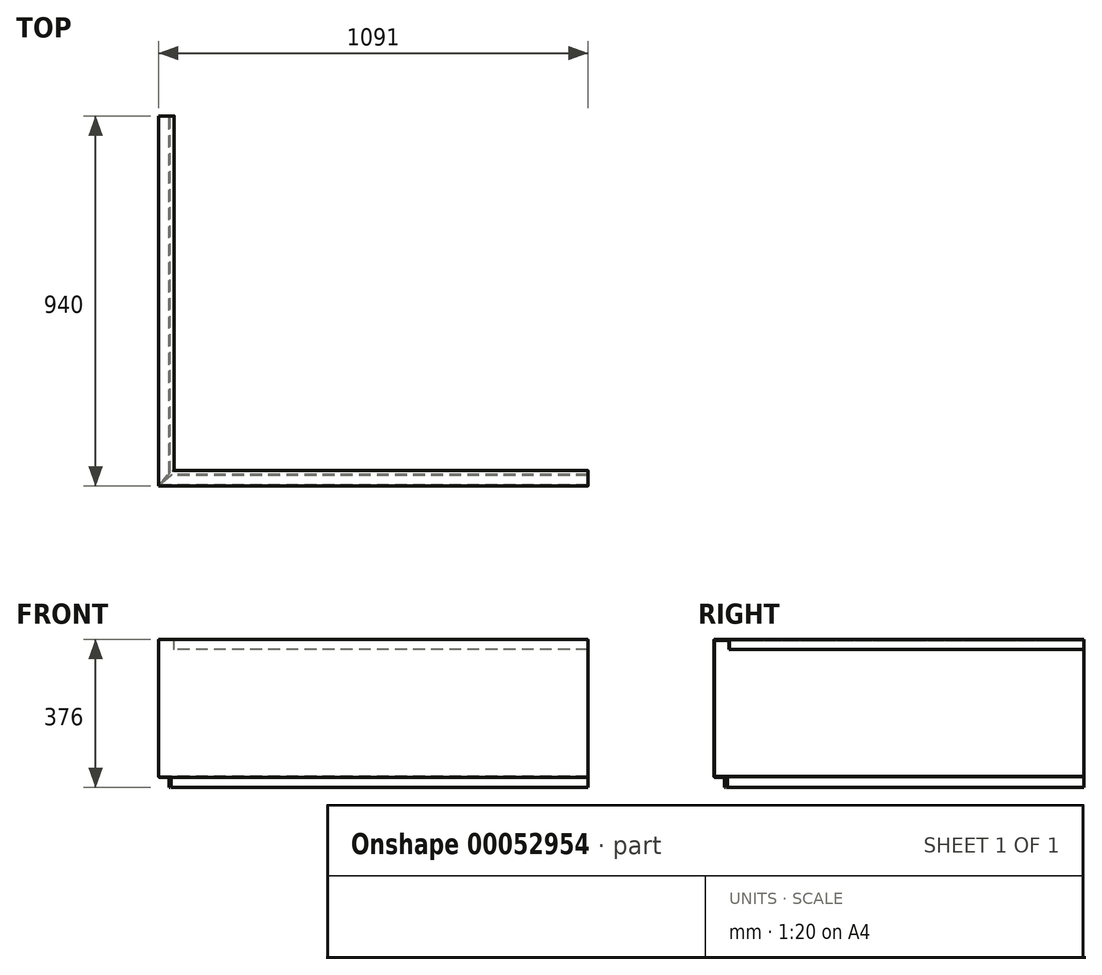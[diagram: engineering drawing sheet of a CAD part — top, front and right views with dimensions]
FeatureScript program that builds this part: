
annotation { "Feature Type Name" : "Feature", "Feature Type Description" : "" }
export const myFeature = defineFeature(function(context is Context, id is Id, definition is map)
    precondition{}
    {
        {
            var Q0;
            Q0=qCreatedBy(makeId("Right.planeOp"),FACE);
            var sketch = newSketch(context, id + "F0", { "sketchPlane" : qUnion([Q0])});
            skLineSegment(sketch, "E0.0", {"start": v(0, -350) * mm, "end": v(27, -350) * mm});
            skLineSegment(sketch, "E0.1", {"start": v(0, 0) * mm, "end": v(0, -350) * mm});
            skLineSegment(sketch, "E1", {"start": v(2, -348) * mm, "end": v(29, -348) * mm});
            skLineSegment(sketch, "E2", {"start": v(2, -2) * mm, "end": v(2, -348) * mm});
            skLineSegment(sketch, "E3", {"start": v(38, -2) * mm, "end": v(2, -2) * mm});
            skLineSegment(sketch, "E4", {"start": v(38, -25) * mm, "end": v(38, -2) * mm});
            skLineSegment(sketch, "E5", {"start": v(27, -350) * mm, "end": v(27, -376) * mm});
            skLineSegment(sketch, "E6", {"start": v(29, -348) * mm, "end": v(29, -376) * mm});
            skLineSegment(sketch, "E0.2", {"start": v(40, 0) * mm, "end": v(0, 0) * mm});
            skLineSegment(sketch, "E0.3", {"start": v(40, -25) * mm, "end": v(40, 0) * mm});
            skLineSegment(sketch, "E7", {"start": v(40, -25) * mm, "end": v(38, -25) * mm});
            skLineSegment(sketch, "E8", {"start": v(29, -376) * mm, "end": v(27, -376) * mm});
            skSolve(sketch);
        }
        {
            var Q0;
            Q0=qCreatedBy(makeId("Top.planeOp"),FACE);
            var sketch = newSketch(context, id + "F1", { "sketchPlane" : qUnion([Q0])});
            skLineSegment(sketch, "E9", {"start": v(0, 0) * mm, "end": v(-1091, 0) * mm});
            skLineSegment(sketch, "E10", {"start": v(-1091, 0) * mm, "end": v(-1091, 940) * mm});
            skSolve(sketch);
        }
        {
            var Q0;
            Q0 = qSketchRegion(id + "F0", true);
            var Q1;
            Q1 = qConstructionFilter(qBodyType(qCreatedBy(id + "F1" ,EDGE), BodyType.WIRE), ConstructionObject.NO);
            sweep(context, id + "F2", {"profiles" : qUnion([Q0]), "path" : qUnion([Q1])});
        }
        {
            var Q0;
            Q0=makeQuery(id+"F2.opSweep","SWEPT_FACE",FACE,{"disambiguationData":[OSD([sQuery(id+"F0.wireOp",EDGE,"E1"),sQuery(id+"F1.wireOp",EDGE,"E9")])]});
            var sketch = newSketch(context, id + "F3", { "sketchPlane" : qUnion([Q0])});
            skLineSegment(sketch, "E11", {"start": v(-1089, 2) * mm, "end": v(-1062, 34.18) * mm});
            skLineSegment(sketch, "E12", {"start": v(-1062, 34.18) * mm, "end": v(-1056.82, 29) * mm});
            skLineSegment(sketch, "E13", {"start": v(-1056.82, 29) * mm, "end": v(-1089, 2) * mm});
            skSolve(sketch);
        }
        {
            var Q0;
            Q0 = qSketchRegion(id + "F3", true);
            extrude(context, id + "F4", {"entities" : qUnion([Q0]), "operationType" : NewBodyOperationType.REMOVE, "oppositeDirection" : true, "depth" : 30 * mm});
        }
        {
            var Q0;
            Q0=makeQuery(id+"F2.opSweep","SWEPT_EDGE",EDGE,{"disambiguationData":[OSD([sQuery(id+"F0.wireOp",EDGE,"E1"),sQuery(id+"F0.wireOp",EDGE,"E6"),sQuery(id+"F1.wireOp",EDGE,"E10")])]});
            var Q1;
            Q1=makeQuery(id+"F2.opSweep","SWEPT_EDGE",EDGE,{"disambiguationData":[OSD([sQuery(id+"F0.wireOp",EDGE,"E1"),sQuery(id+"F0.wireOp",EDGE,"E2"),sQuery(id+"F1.wireOp",EDGE,"E10")])]});
            var Q2;
            Q2=makeQuery(id+"F2.opSweep","SWEPT_EDGE",EDGE,{"disambiguationData":[OSD([sQuery(id+"F0.wireOp",EDGE,"E0.2"),sQuery(id+"F0.wireOp",EDGE,"E0.3"),sQuery(id+"F1.wireOp",EDGE,"E10")])]});
            var Q3;
            Q3=makeQuery(id+"F2.opSweep","SWEPT_EDGE",EDGE,{"disambiguationData":[OSD([sQuery(id+"F0.wireOp",EDGE,"E0.0"),sQuery(id+"F0.wireOp",EDGE,"E5"),sQuery(id+"F1.wireOp",EDGE,"E10")])]});
            var Q4;
            Q4=makeQuery(id+"F2.opSweep","SWEPT_EDGE",EDGE,{"disambiguationData":[OSD([sQuery(id+"F0.wireOp",EDGE,"E0.0"),sQuery(id+"F0.wireOp",EDGE,"E0.1"),sQuery(id+"F1.wireOp",EDGE,"E10")])]});
            var Q5;
            Q5=makeQuery(id+"F2.opSweep","SWEPT_EDGE",EDGE,{"disambiguationData":[OSD([sQuery(id+"F0.wireOp",EDGE,"E0.1"),sQuery(id+"F0.wireOp",EDGE,"E0.2"),sQuery(id+"F1.wireOp",EDGE,"E10")])]});
            var Q6;
            Q6=makeQuery(id+"F2.opSweep","SWEPT_EDGE",EDGE,{"disambiguationData":[OSD([sQuery(id+"F0.wireOp",EDGE,"E3"),sQuery(id+"F0.wireOp",EDGE,"E4"),sQuery(id+"F1.wireOp",EDGE,"E10")])]});
            var Q7;
            Q7=makeQuery(id+"F2.opSweep","SWEPT_EDGE",EDGE,{"disambiguationData":[OSD([sQuery(id+"F0.wireOp",EDGE,"E2"),sQuery(id+"F0.wireOp",EDGE,"E3"),sQuery(id+"F1.wireOp",EDGE,"E10")])]});
            var Q8;
            Q8=makeQuery(id+"F2.opSweep","SWEPT_EDGE",EDGE,{"disambiguationData":[OSD([sQuery(id+"F0.wireOp",EDGE,"E0.0"),sQuery(id+"F0.wireOp",EDGE,"E5"),sQuery(id+"F1.wireOp",EDGE,"E9")])]});
            var Q9;
            Q9=makeQuery(id+"F2.opSweep","SWEPT_EDGE",EDGE,{"disambiguationData":[OSD([sQuery(id+"F0.wireOp",EDGE,"E1"),sQuery(id+"F0.wireOp",EDGE,"E6"),sQuery(id+"F1.wireOp",EDGE,"E9")])]});
            var Q10;
            Q10=makeQuery(id+"F2.opSweep","SWEPT_EDGE",EDGE,{"disambiguationData":[OSD([sQuery(id+"F0.wireOp",EDGE,"E0.0"),sQuery(id+"F0.wireOp",EDGE,"E0.1"),sQuery(id+"F1.wireOp",EDGE,"E9")])]});
            var Q11;
            Q11=makeQuery(id+"F2.opSweep","SWEPT_EDGE",EDGE,{"disambiguationData":[OSD([sQuery(id+"F0.wireOp",EDGE,"E1"),sQuery(id+"F0.wireOp",EDGE,"E2"),sQuery(id+"F1.wireOp",EDGE,"E9")])]});
            var Q12;
            Q12=makeQuery(id+"F2.opSweep","SWEPT_EDGE",EDGE,{"disambiguationData":[OSD([sQuery(id+"F0.wireOp",EDGE,"E0.2"),sQuery(id+"F0.wireOp",EDGE,"E0.3"),sQuery(id+"F1.wireOp",EDGE,"E9")])]});
            var Q13;
            Q13=makeQuery(id+"F2.opSweep","SWEPT_EDGE",EDGE,{"disambiguationData":[OSD([sQuery(id+"F0.wireOp",EDGE,"E0.1"),sQuery(id+"F0.wireOp",EDGE,"E0.2"),sQuery(id+"F1.wireOp",EDGE,"E9")])]});
            var Q14;
            Q14=makeQuery(id+"F2.opSweep","SWEPT_EDGE",EDGE,{"disambiguationData":[OSD([sQuery(id+"F0.wireOp",EDGE,"E2"),sQuery(id+"F0.wireOp",EDGE,"E3"),sQuery(id+"F1.wireOp",EDGE,"E9")])]});
            var Q15;
            Q15=makeQuery(id+"F2.opSweep","SWEPT_EDGE",EDGE,{"disambiguationData":[OSD([sQuery(id+"F0.wireOp",EDGE,"E3"),sQuery(id+"F0.wireOp",EDGE,"E4"),sQuery(id+"F1.wireOp",EDGE,"E9")])]});
            fillet(context, id + "F5", {"entities" : qUnion([Q0, Q1, Q2, Q3, Q4, Q5, Q6, Q7, Q8, Q9, Q10, Q11, Q12, Q13, Q14, Q15]), "radius" : 2 * mm, "tangentPropagation" : true, "allowEdgeOverflow" : false});
        }
    });
